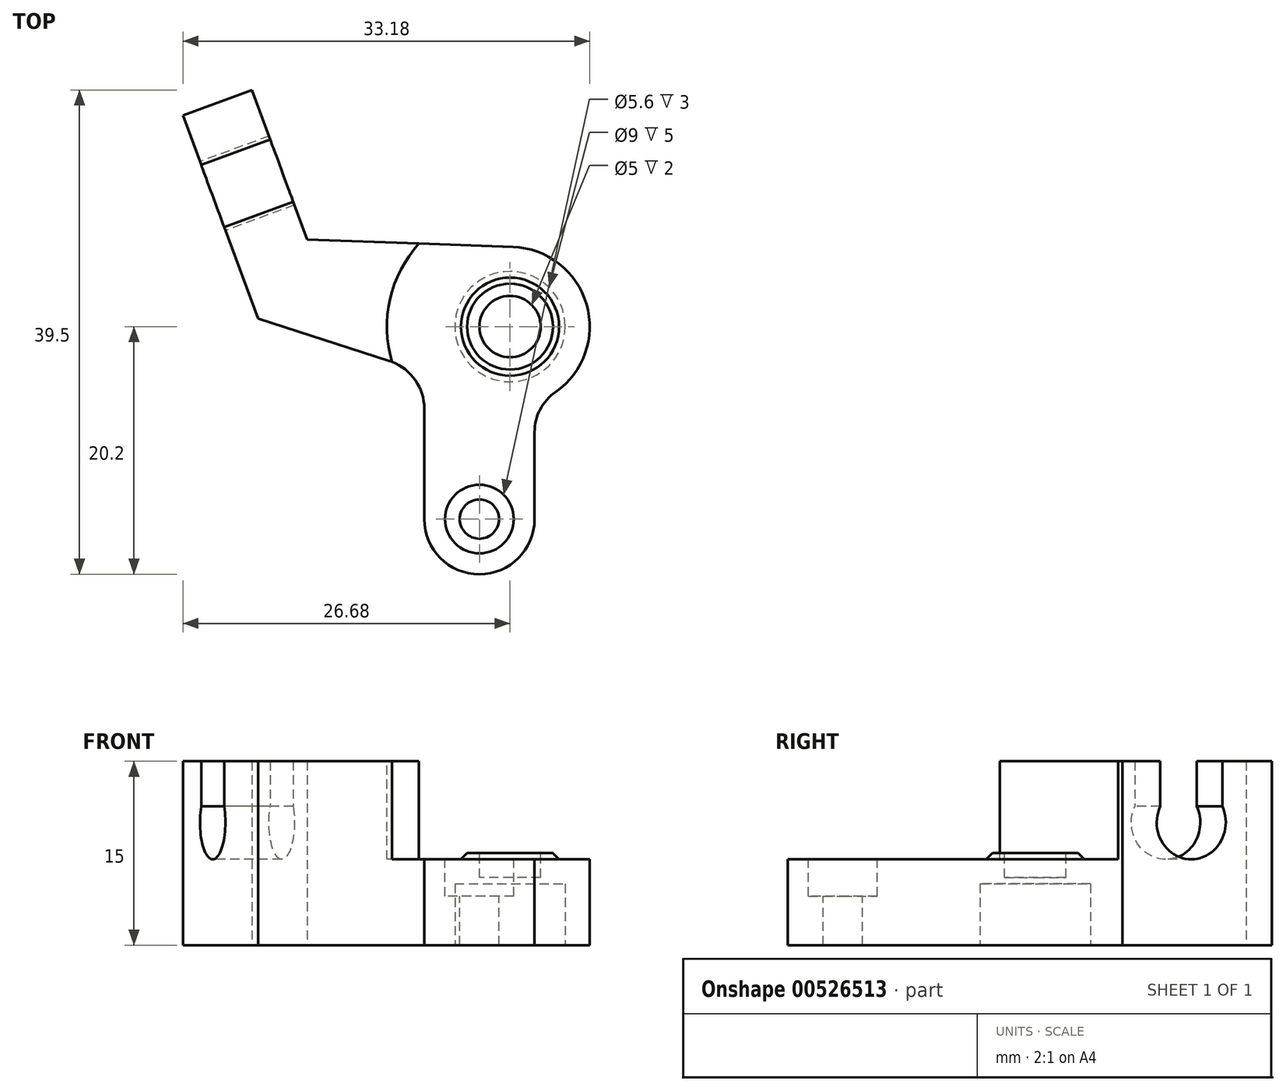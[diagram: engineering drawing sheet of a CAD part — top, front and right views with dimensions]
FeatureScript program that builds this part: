
annotation { "Feature Type Name" : "Feature", "Feature Type Description" : "" }
export const myFeature = defineFeature(function(context is Context, id is Id, definition is map)
    precondition{}
    {
        {
            var Q0;
            Q0=qCreatedBy(makeId("Top.planeOp"),FACE);
            var sketch = newSketch(context, id + "F0", { "sketchPlane" : qUnion([Q0])});
            skArc(sketch, "E0", {"start": v(2, -6.18) * mm, "mid": v(6.44, 0.9) * mm, "end": v(0.23, 6.5) * mm});
            skLineSegment(sketch, "E1", {"start": v(-26.68, 17.22) * mm, "end": v(-21.06, 19.3) * mm});
            skLineSegment(sketch, "E2", {"start": v(-21.06, 19.3) * mm, "end": v(-16.56, 7.1) * mm});
            skLineSegment(sketch, "E3", {"start": v(-16.56, 7.1) * mm, "end": v(0.23, 6.5) * mm});
            skLineSegment(sketch, "E4", {"start": v(2, -6.18) * mm, "end": v(2, -15.7) * mm});
            skArc(sketch, "E5", {"start": v(2, -15.7) * mm, "mid": v(-2.5, -20.2) * mm, "end": v(-7, -15.7) * mm});
            skLineSegment(sketch, "E6", {"start": v(-7, -15.7) * mm, "end": v(-7, -6.7) * mm});
            skLineSegment(sketch, "E7", {"start": v(-20.57, 0.64) * mm, "end": v(-26.68, 17.22) * mm});
            skLineSegment(sketch, "E8", {"start": v(-20.57, 0.64) * mm, "end": v(-9.85, -2.8) * mm});
            skArc(sketch, "E9", {"start": v(-9.85, -2.8) * mm, "mid": v(-7.79, -4.28) * mm, "end": v(-7, -6.7) * mm});
            skSolve(sketch);
        }
        {
            var Q0;
            Q0 = qSketchRegion(id + "F0", true);
            extrude(context, id + "F1", {"entities" : qUnion([Q0]), "depth" : 15 * mm, "offsetDistance" : 25 * mm});
        }
        {
            var Q0;
            Q0=makeQuery(id+"F1.opExtrude","CAP_FACE",FACE,{"disambiguationData":[OSD([sQuery(id+"F0.wireOp",EDGE,"E0"),sQuery(id+"F0.wireOp",EDGE,"E1"),sQuery(id+"F0.wireOp",EDGE,"E2"),sQuery(id+"F0.wireOp",EDGE,"E3"),sQuery(id+"F0.wireOp",EDGE,"E4"),sQuery(id+"F0.wireOp",EDGE,"E5"),sQuery(id+"F0.wireOp",EDGE,"E6"),sQuery(id+"F0.wireOp",EDGE,"E7"),sQuery(id+"F0.wireOp",EDGE,"E8"),sQuery(id+"F0.wireOp",EDGE,"E9")])],"isStart":false});
            var sketch = newSketch(context, id + "F2", { "sketchPlane" : qUnion([Q0])});
            skArc(sketch, "E10", {"start": v(2, -9.85) * mm, "mid": v(2.83, 9.64) * mm, "end": v(-7, -7.21) * mm});
            skLineSegment(sketch, "E11.0", {"start": v(-7, -15.7) * mm, "end": v(-7, -7.21) * mm});
            skArc(sketch, "E12.0", {"start": v(2, -15.7) * mm, "mid": v(-2.5, -20.2) * mm, "end": v(-7, -15.7) * mm});
            skLineSegment(sketch, "E13.0", {"start": v(2, -9.85) * mm, "end": v(2, -15.7) * mm});
            skSolve(sketch);
        }
        {
            var Q0;
            Q0 = qSketchRegion(id + "F2", true);
            extrude(context, id + "F3", {"entities" : qUnion([Q0]), "operationType" : NewBodyOperationType.REMOVE, "oppositeDirection" : true, "depth" : 8 * mm, "offsetDistance" : 25 * mm});
        }
        {
            var Q0;
            Q0=makeQuery(id+"F3.boolean.opBoolean","COPY",FACE,{"derivedFrom":makeQuery(id+"F3.opExtrude","CAP_FACE",FACE,{"disambiguationData":[OSD([sQuery(id+"F2.wireOp",EDGE,"E10"),sQuery(id+"F2.wireOp",EDGE,"E11.0"),sQuery(id+"F2.wireOp",EDGE,"E12.0"),sQuery(id+"F2.wireOp",EDGE,"E13.0")])],"isStart":false})});
            var sketch = newSketch(context, id + "F4", { "sketchPlane" : qUnion([Q0])});
            skPoint(sketch, "E14", {"position": v(-2.5, -15.7) * mm});
            skSolve(sketch);
        }
        {
            var Q0;
            Q0=sQuery(id+"F4.wireOp",VERTEX,"E14");
            var Q1;
            Q1=makeQuery(id+"F1.opExtrude","SWEPT_BODY",BODY,{"disambiguationData":[OSD([sQuery(id+"F0.wireOp",EDGE,"E0"),sQuery(id+"F0.wireOp",EDGE,"E1"),sQuery(id+"F0.wireOp",EDGE,"E2"),sQuery(id+"F0.wireOp",EDGE,"E3"),sQuery(id+"F0.wireOp",EDGE,"E4"),sQuery(id+"F0.wireOp",EDGE,"E5"),sQuery(id+"F0.wireOp",EDGE,"E6"),sQuery(id+"F0.wireOp",EDGE,"E7"),sQuery(id+"F0.wireOp",EDGE,"E8"),sQuery(id+"F0.wireOp",EDGE,"E9")])]});
            hole(context, id + "F5", {"style" : HoleStyle.C_BORE, "endStyle" : HoleEndStyle.THROUGH, "holeDiameter" : 3.2 * mm, "cBoreDiameter" : 5.6 * mm, "cBoreDepth" : 3 * mm, "isTappedThrough" : true, "tappedDepth" : 12 * mm, "tapClearance" : 3, "locations" : qUnion([Q0]), "scope" : qUnion([Q1])});
        }
        {
            var Q0;
            Q0=makeQuery(id+"F1.opExtrude","CAP_FACE",FACE,{"disambiguationData":[OSD([sQuery(id+"F0.wireOp",EDGE,"E0"),sQuery(id+"F0.wireOp",EDGE,"E1"),sQuery(id+"F0.wireOp",EDGE,"E2"),sQuery(id+"F0.wireOp",EDGE,"E3"),sQuery(id+"F0.wireOp",EDGE,"E4"),sQuery(id+"F0.wireOp",EDGE,"E5"),sQuery(id+"F0.wireOp",EDGE,"E6"),sQuery(id+"F0.wireOp",EDGE,"E7"),sQuery(id+"F0.wireOp",EDGE,"E8"),sQuery(id+"F0.wireOp",EDGE,"E9")])],"isStart":true});
            var sketch = newSketch(context, id + "F6", { "sketchPlane" : qUnion([Q0])});
            skCircle(sketch, "E15", {"center": v(0, 0) * mm, "radius": 4.5 * mm});
            skSolve(sketch);
        }
        {
            var Q0;
            Q0 = qSketchRegion(id + "F6", true);
            extrude(context, id + "F7", {"entities" : qUnion([Q0]), "operationType" : NewBodyOperationType.REMOVE, "oppositeDirection" : true, "depth" : 5 * mm, "offsetDistance" : 25 * mm});
        }
        {
            var Q0;
            Q0=makeQuery(id+"F3.boolean.opBoolean","COPY",FACE,{"derivedFrom":makeQuery(id+"F3.opExtrude","CAP_FACE",FACE,{"disambiguationData":[OSD([sQuery(id+"F2.wireOp",EDGE,"E10"),sQuery(id+"F2.wireOp",EDGE,"E11.0"),sQuery(id+"F2.wireOp",EDGE,"E12.0"),sQuery(id+"F2.wireOp",EDGE,"E13.0")])],"isStart":false})});
            var sketch = newSketch(context, id + "F8", { "sketchPlane" : qUnion([Q0])});
            skCircle(sketch, "E16", {"center": v(0, 0) * mm, "radius": 4 * mm});
            skSolve(sketch);
        }
        {
            var Q0;
            Q0 = qSketchRegion(id + "F8", true);
            extrude(context, id + "F9", {"entities" : qUnion([Q0]), "operationType" : NewBodyOperationType.ADD, "depth" : 0.5 * mm, "offsetDistance" : 25 * mm});
        }
        {
            var Q0;
            Q0=makeQuery(id+"F9.opExtrude","CAP_FACE",FACE,{"disambiguationData":[OSD([sQuery(id+"F8.wireOp",EDGE,"E16")])],"isStart":false});
            var sketch = newSketch(context, id + "F10", { "sketchPlane" : qUnion([Q0])});
            skCircle(sketch, "E17", {"center": v(0, 0) * mm, "radius": 2.5 * mm});
            skSolve(sketch);
        }
        {
            var Q0;
            Q0 = qSketchRegion(id + "F10", true);
            extrude(context, id + "F11", {"entities" : qUnion([Q0]), "operationType" : NewBodyOperationType.REMOVE, "oppositeDirection" : true, "depth" : 2 * mm, "offsetDistance" : 25 * mm});
        }
        {
            var Q0;
            Q0=makeQuery(id+"F9.opExtrude","CAP_EDGE",EDGE,{"disambiguationData":[OSD([sQuery(id+"F8.wireOp",EDGE,"E16")])],"isStart":false});
            chamfer(context, id + "F12", {"entities" : qUnion([Q0]), "width" : 0.5 * mm, "tangentPropagation" : true});
        }
        {
            var Q0;
            Q0=makeQuery(id+"F1.opExtrude","SWEPT_FACE",FACE,{"disambiguationData":[OSD([sQuery(id+"F0.wireOp",EDGE,"E7")])]});
            var sketch = newSketch(context, id + "F13", { "sketchPlane" : qUnion([Q0])});
            skLineSegment(sketch, "E18", {"start": v(-21.1, 15) * mm, "end": v(-21.1, 11.3) * mm});
            skLineSegment(sketch, "E19", {"start": v(-21.1, 15) * mm, "end": v(-15.7, 15) * mm});
            skLineSegment(sketch, "E20", {"start": v(-15.7, 15) * mm, "end": v(-15.7, 11.3) * mm});
            skArc(sketch, "E21", {"start": v(-21.1, 11.3) * mm, "mid": v(-18.4, 7) * mm, "end": v(-15.7, 11.3) * mm});
            skLineSegment(sketch, "E22", {"start": v(-18.4, 10) * mm, "end": v(-18.4, 15) * mm, "construction": true});
            skSolve(sketch);
        }
        {
            var Q0;
            Q0 = qSketchRegion(id + "F13", true);
            extrude(context, id + "F14", {"entities" : qUnion([Q0]), "operationType" : NewBodyOperationType.REMOVE, "endBound" : BoundingType.UP_TO_NEXT, "oppositeDirection" : true, "depth" : 25 * mm, "offsetDistance" : 25 * mm});
        }
        {
            var Q0;
            Q0=makeQuery(id+"F1.opExtrude","SWEPT_EDGE",EDGE,{"disambiguationData":[OSD([sQuery(id+"F0.wireOp",EDGE,"E0"),sQuery(id+"F0.wireOp",EDGE,"E4")])]});
            fillet(context, id + "F15", {"entities" : qUnion([Q0]), "radius" : 4 * mm, "tangentPropagation" : true, "allowEdgeOverflow" : false});
        }
    });
